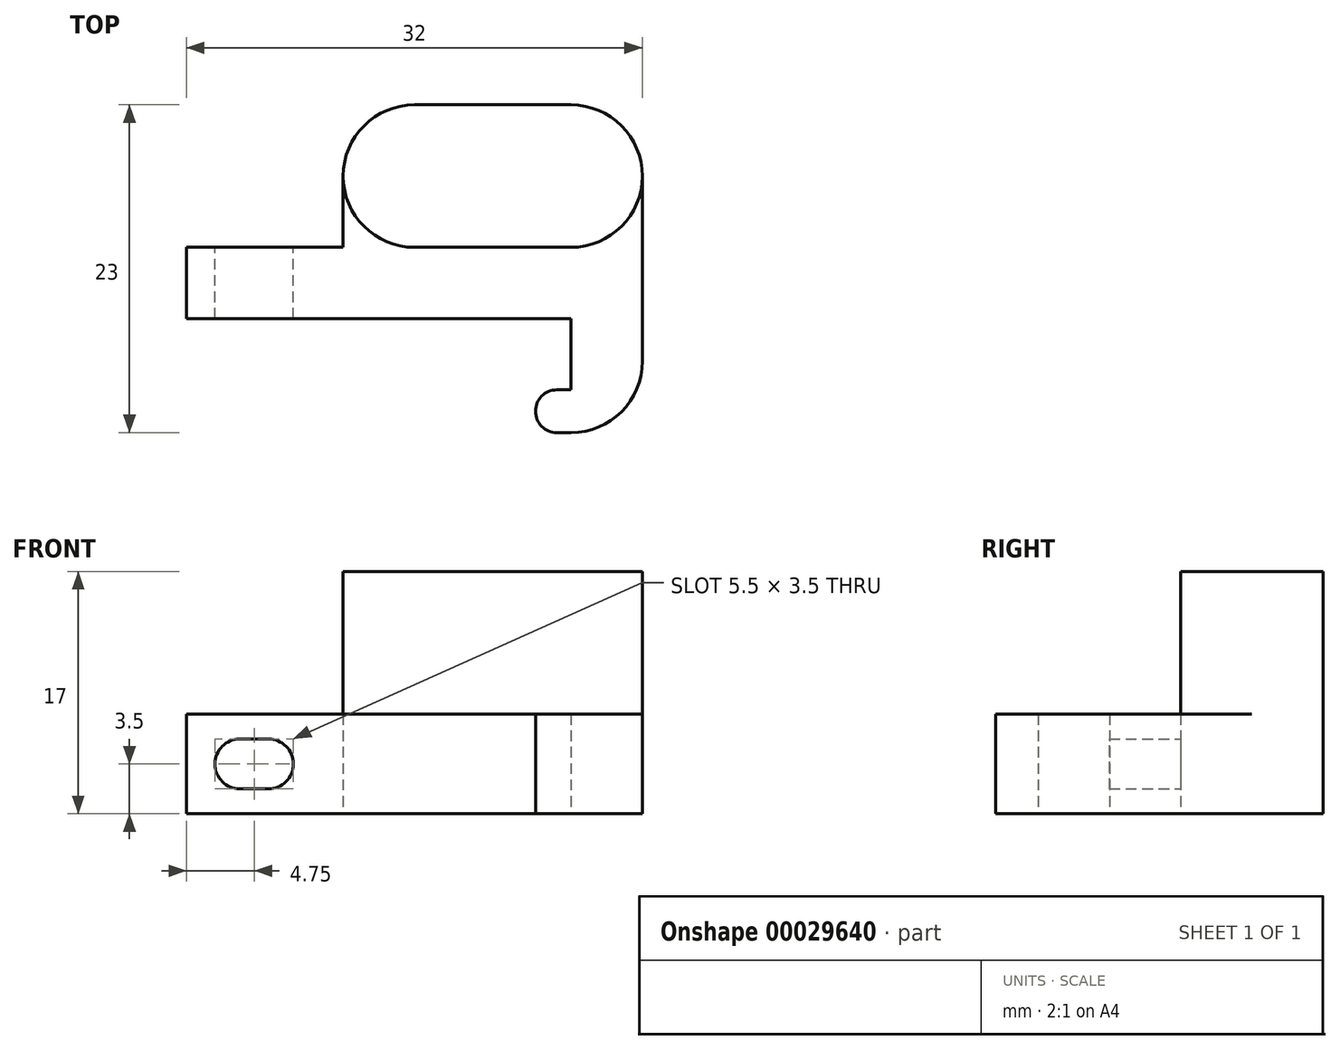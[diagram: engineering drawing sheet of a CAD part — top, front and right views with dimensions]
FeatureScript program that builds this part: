
annotation { "Feature Type Name" : "Feature", "Feature Type Description" : "" }
export const myFeature = defineFeature(function(context is Context, id is Id, definition is map)
    precondition{}
    {
        {
            var Q0;
            Q0=qCreatedBy(makeId("Top.planeOp"),FACE);
            var sketch = newSketch(context, id + "F0", { "sketchPlane" : qUnion([Q0])});
            skLineSegment(sketch, "E0", {"start": v(0, 0) * mm, "end": v(5, 0) * mm});
            skLineSegment(sketch, "E1", {"start": v(5, 0) * mm, "end": v(5, 13) * mm});
            skLineSegment(sketch, "E2", {"start": v(5, 13) * mm, "end": v(-27, 13) * mm});
            skLineSegment(sketch, "E3", {"start": v(-27, 13) * mm, "end": v(-27, 8) * mm});
            skLineSegment(sketch, "E4", {"start": v(-27, 8) * mm, "end": v(0, 8) * mm});
            skLineSegment(sketch, "E5", {"start": v(0, 8) * mm, "end": v(0, 3) * mm});
            skLineSegment(sketch, "E6", {"start": v(0, 3) * mm, "end": v(-1, 3) * mm});
            skLineSegment(sketch, "E7", {"start": v(0, 0) * mm, "end": v(-1, 0) * mm});
            skArc(sketch, "E8", {"start": v(-1, 3) * mm, "mid": v(-2.5, 1.5) * mm, "end": v(-1, 0) * mm});
            skSolve(sketch);
        }
        {
            var Q0;
            Q0=qSketchRegion(id+"F0",true);
            extrude(context, id + "F1", {"entities" : qUnion([Q0]), "depth" : 7 * mm});
        }
        {
            var Q0;
            Q0=makeQuery(id+"F1.opExtrude","SWEPT_FACE",FACE,{"disambiguationData":[OSD([sQuery(id+"F0.wireOp",EDGE,"E2")])]});
            var sketch = newSketch(context, id + "F2", { "sketchPlane" : qUnion([Q0])});
            skCircle(sketch, "E9", {"center": v(23.25, 3.5) * mm, "radius": 1.75 * mm});
            skLineSegment(sketch, "E10", {"start": v(23.25, 7) * mm, "end": v(23.25, 0) * mm});
            skCircle(sketch, "E11", {"center": v(21.25, 3.5) * mm, "radius": 1.75 * mm});
            skLineSegment(sketch, "E12", {"start": v(21.25, 5.25) * mm, "end": v(23.25, 5.25) * mm});
            skLineSegment(sketch, "E13", {"start": v(21.25, 1.75) * mm, "end": v(23.25, 1.75) * mm});
            skSolve(sketch);
        }
        {
            var Q0;
            Q0=qSketchRegion(id+"F2",true);
            var Q1;
            {var subQ0=sQuery(id+"F2.wireOp",EDGE,"E11");var subQ1=sQuery(id+"F2.wireOp",EDGE,"E9");var subQ3=makeQuery(id+"F2.imprint","INTERSECT",VERTEX,{"disambiguationData":[OD(0.0)],"derivedFrom":[subQ1,subQ0]});Q1=makeQuery(id+"F2.imprint","IMPRINT",FACE,{"disambiguationData":[TD([[makeQuery(id+"F2.imprint","IMPRINT",EDGE,{"disambiguationData":[TD([[subQ3,-1.0]])],"derivedFrom":subQ1}),1.0]])]});}
            extrude(context, id + "F3", {"entities" : qUnion([Q0, Q1]), "operationType" : NewBodyOperationType.REMOVE, "oppositeDirection" : true, "depth" : 25 * mm, "hasSecondDirection" : true, "secondDirectionOppositeDirection" : false, "secondDirectionDepth" : 25 * mm});
        }
        {
            var Q0;
            Q0=makeQuery(id+"F1.opExtrude","SWEPT_FACE",FACE,{"disambiguationData":[OSD([sQuery(id+"F0.wireOp",EDGE,"E2")])]});
            var sketch = newSketch(context, id + "F4", { "sketchPlane" : qUnion([Q0])});
            skLineSegment(sketch, "E14.bottom", {"start": v(-5, 7) * mm, "end": v(16, 7) * mm});
            skLineSegment(sketch, "E14.top", {"start": v(-5, 0) * mm, "end": v(16, 0) * mm});
            skLineSegment(sketch, "E14.left", {"start": v(-5, 7) * mm, "end": v(-5, 0) * mm});
            skLineSegment(sketch, "E14.right", {"start": v(16, 7) * mm, "end": v(16, 0) * mm});
            skSolve(sketch);
        }
        {
            var Q0;
            Q0=qSketchRegion(id+"F4",true);
            extrude(context, id + "F5", {"entities" : qUnion([Q0]), "operationType" : NewBodyOperationType.ADD, "depth" : 10 * mm});
        }
        {
            var Q0;
            Q0=makeQuery(id+"F5.opExtrude","CAP_EDGE",EDGE,{"disambiguationData":[OSD([sQuery(id+"F4.wireOp",EDGE,"E14.left")])],"isStart":false});
            var Q1;
            Q1=makeQuery(id+"F5.opExtrude","CAP_EDGE",EDGE,{"disambiguationData":[OSD([sQuery(id+"F4.wireOp",EDGE,"E14.right")])],"isStart":false});
            fillet(context, id + "F6", {"entities" : qUnion([Q0, Q1]), "radius" : 5 * mm, "tangentPropagation" : true, "allowEdgeOverflow" : false});
        }
        {
            var Q0;
            Q0=makeQuery(id+"F1.opExtrude","SWEPT_EDGE",EDGE,{"disambiguationData":[OSD([sQuery(id+"F0.wireOp",EDGE,"E0"),sQuery(id+"F0.wireOp",EDGE,"E1")])]});
            fillet(context, id + "F7", {"entities" : qUnion([Q0]), "radius" : 5 * mm, "tangentPropagation" : true, "allowEdgeOverflow" : false});
        }
        {
            var Q0;
            Q0=makeQuery(id+"F5.boolean.opBoolean","MERGE",FACE,{"derivedFrom":[makeQuery(id+"F1.opExtrude","CAP_FACE",FACE,{"disambiguationData":[OSD([sQuery(id+"F0.wireOp",EDGE,"E0"),sQuery(id+"F0.wireOp",EDGE,"E1"),sQuery(id+"F0.wireOp",EDGE,"E2"),sQuery(id+"F0.wireOp",EDGE,"E3"),sQuery(id+"F0.wireOp",EDGE,"E4"),sQuery(id+"F0.wireOp",EDGE,"E5"),sQuery(id+"F0.wireOp",EDGE,"E6"),sQuery(id+"F0.wireOp",EDGE,"E7"),sQuery(id+"F0.wireOp",EDGE,"E8")])],"isStart":false}),makeQuery(id+"F5.opExtrude","SWEPT_FACE",FACE,{"disambiguationData":[OSD([sQuery(id+"F4.wireOp",EDGE,"E14.bottom")])]})]});
            var sketch = newSketch(context, id + "F8", { "sketchPlane" : qUnion([Q0])});
            skLineSegment(sketch, "E15.bottom", {"start": v(-11, 13) * mm, "end": v(0, 13) * mm});
            skLineSegment(sketch, "E15.top", {"start": v(-11, 23) * mm, "end": v(0, 23) * mm});
            skLineSegment(sketch, "E15.left", {"start": v(-16, 18) * mm, "end": v(-16, 18) * mm});
            skLineSegment(sketch, "E15.right", {"start": v(5, 18) * mm, "end": v(5, 18) * mm});
            skPoint(sketch, "E16.visualSharp", {"position": v(-16, 23) * mm});
            skArc(sketch, "E16.filletArc", {"start": v(-11, 23) * mm, "mid": v(-14.54, 21.54) * mm, "end": v(-16, 18) * mm});
            skPoint(sketch, "E17.visualSharp", {"position": v(5, 23) * mm});
            skArc(sketch, "E17.filletArc", {"start": v(5, 18) * mm, "mid": v(3.54, 21.54) * mm, "end": v(0, 23) * mm});
            skPoint(sketch, "E18.visualSharp", {"position": v(-16, 13) * mm});
            skArc(sketch, "E18.filletArc", {"start": v(-16, 18) * mm, "mid": v(-14.54, 14.46) * mm, "end": v(-11, 13) * mm});
            skPoint(sketch, "E19.visualSharp", {"position": v(5, 13) * mm});
            skArc(sketch, "E19.filletArc", {"start": v(0, 13) * mm, "mid": v(3.54, 14.46) * mm, "end": v(5, 18) * mm});
            skSolve(sketch);
        }
        {
            var Q0;
            Q0=makeQuery(id+"F8.imprint","IMPRINT",FACE,{"disambiguationData":[TD([[makeQuery(id+"F8.imprint","IMPRINT",EDGE,{"derivedFrom":sQuery(id+"F8.wireOp",EDGE,"E15.bottom")}),1.0]])]});
            extrude(context, id + "F9", {"entities" : qUnion([Q0]), "operationType" : NewBodyOperationType.ADD, "depth" : 10 * mm});
        }
    });
